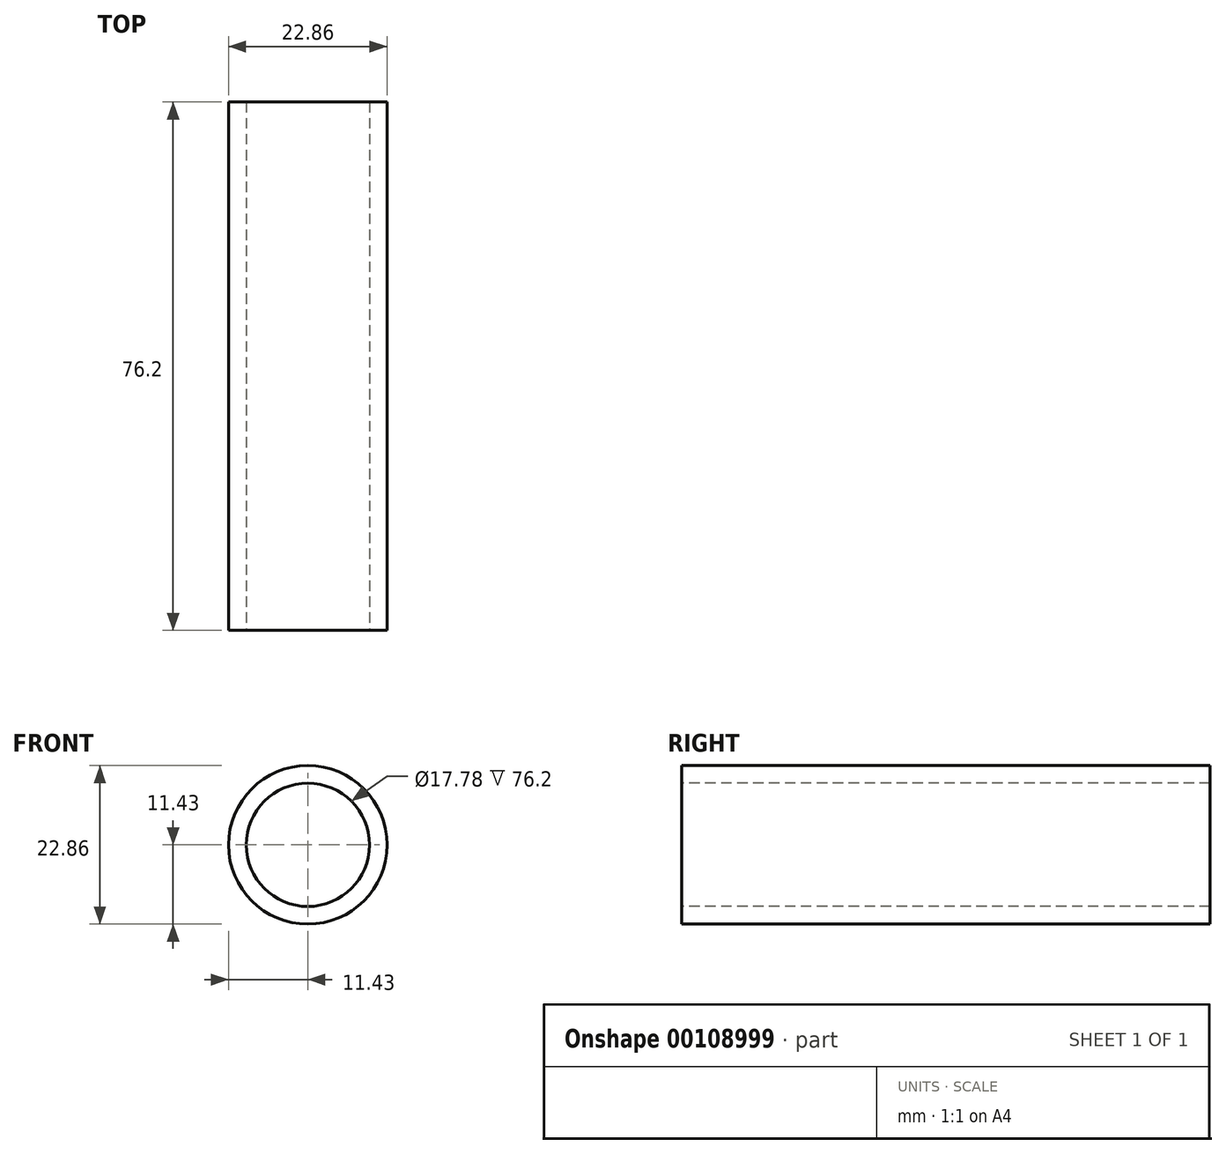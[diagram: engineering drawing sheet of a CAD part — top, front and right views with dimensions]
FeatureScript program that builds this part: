
annotation { "Feature Type Name" : "Feature", "Feature Type Description" : "" }
export const myFeature = defineFeature(function(context is Context, id is Id, definition is map)
    precondition{}
    {
        {
            var Q0;
            Q0=qCreatedBy(makeId("Front.planeOp"),FACE);
            var sketch = newSketch(context, id + "F0", { "sketchPlane" : qUnion([Q0])});
            skCircle(sketch, "E0", {"center": v(0, 0) * mm, "radius": 8.9 * mm});
            skCircle(sketch, "E1", {"center": v(0, 0) * mm, "radius": 11.43 * mm});
            skSolve(sketch);
        }
        {
            var Q0;
            Q0=makeQuery(id+"F0.imprint","IMPRINT",FACE,{"disambiguationData":[TD([[makeQuery(id+"F0.imprint","IMPRINT",EDGE,{"derivedFrom":sQuery(id+"F0.wireOp",EDGE,"E0")}),-1.0]])]});
            extrude(context, id + "F1", {"entities" : qUnion([Q0]), "oppositeDirection" : true, "depth" : 76.2 * mm});
        }
    });
